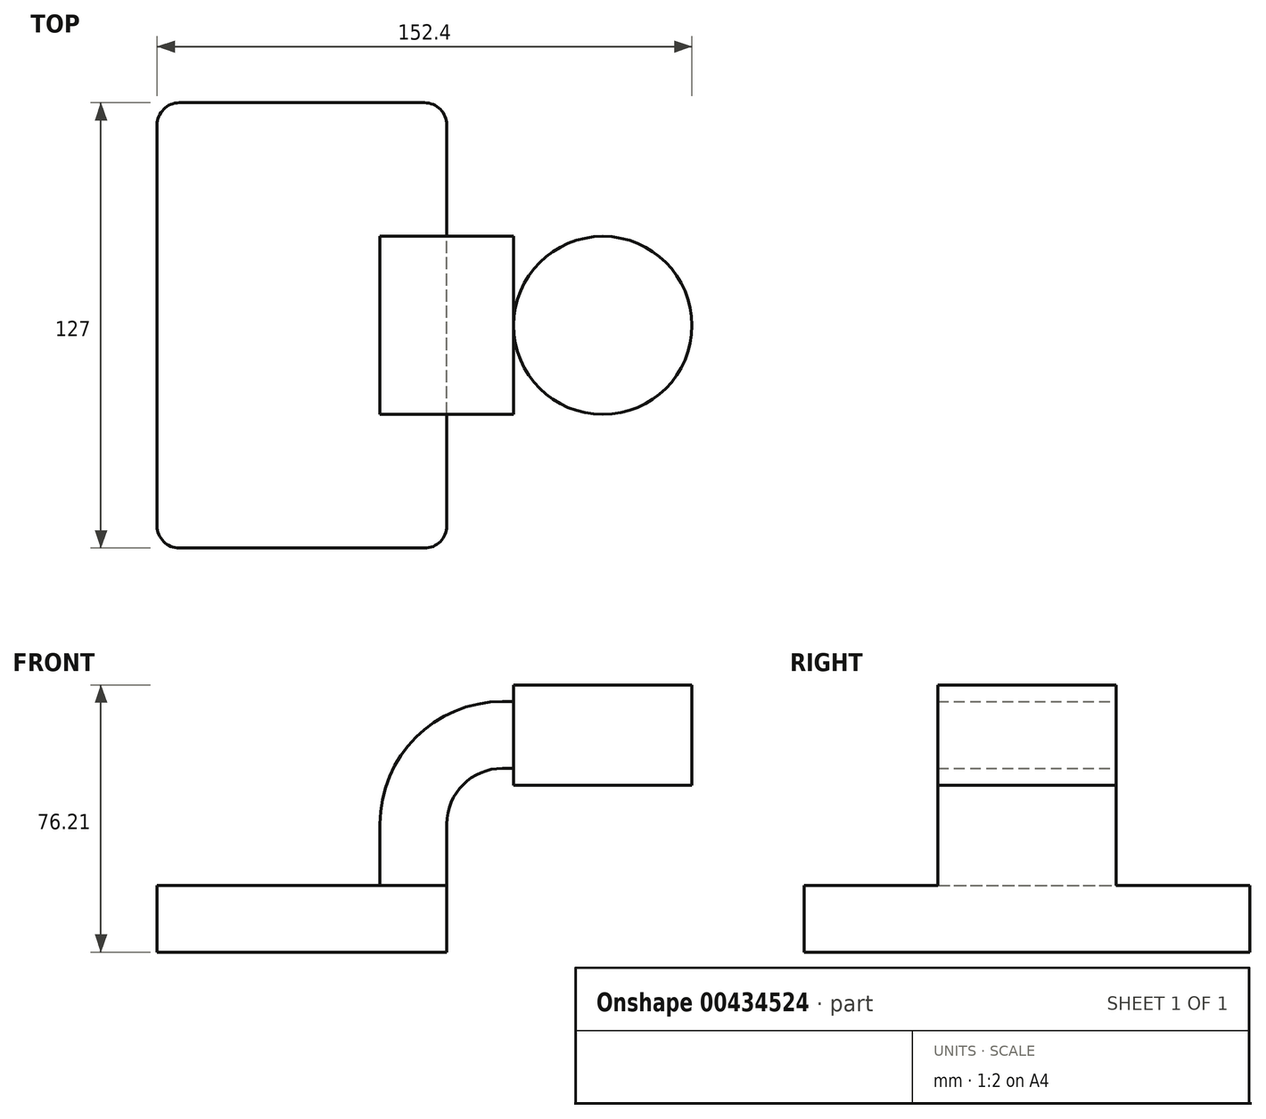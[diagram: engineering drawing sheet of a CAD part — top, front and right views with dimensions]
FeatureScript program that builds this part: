
annotation { "Feature Type Name" : "Feature", "Feature Type Description" : "" }
export const myFeature = defineFeature(function(context is Context, id is Id, definition is map)
    precondition{}
    {
        {
            var Q0;
            Q0=qCreatedBy(makeId("Front.planeOp"),FACE);
            var sketch = newSketch(context, id + "F0", { "sketchPlane" : qUnion([Q0])});
            skLineSegment(sketch, "E0.bottom", {"start": v(-41.28, 9.52) * mm, "end": v(41.27, 9.53) * mm});
            skLineSegment(sketch, "E0.top", {"start": v(-41.28, -9.53) * mm, "end": v(41.28, -9.53) * mm});
            skLineSegment(sketch, "E0.left", {"start": v(-41.28, 9.52) * mm, "end": v(-41.27, -9.53) * mm});
            skLineSegment(sketch, "E0.right", {"start": v(41.28, 9.53) * mm, "end": v(41.28, -9.52) * mm});
            skPoint(sketch, "E0.middle", {"position": v(0, 0) * mm});
            skLineSegment(sketch, "E1.bottom", {"start": v(111.13, 66.68) * mm, "end": v(60.33, 66.68) * mm});
            skLineSegment(sketch, "E1.top", {"start": v(111.13, 38.1) * mm, "end": v(60.33, 38.1) * mm});
            skLineSegment(sketch, "E1.left", {"start": v(111.13, 66.68) * mm, "end": v(111.13, 38.1) * mm});
            skLineSegment(sketch, "E1.right", {"start": v(60.33, 66.68) * mm, "end": v(60.33, 38.1) * mm});
            skPoint(sketch, "E1.middle", {"position": v(85.73, 52.39) * mm});
            skLineSegment(sketch, "E2", {"start": v(41.27, 9.53) * mm, "end": v(41.27, 27) * mm});
            skArc(sketch, "E3", {"start": v(41.27, 27) * mm, "mid": v(45.92, 38.23) * mm, "end": v(57.15, 42.88) * mm});
            skLineSegment(sketch, "E4", {"start": v(57.15, 42.88) * mm, "end": v(85.72, 42.88) * mm});
            skLineSegment(sketch, "E5.0", {"start": v(57.15, 61.93) * mm, "end": v(85.73, 61.93) * mm});
            skArc(sketch, "E5.1", {"start": v(22.22, 27) * mm, "mid": v(32.45, 51.7) * mm, "end": v(57.15, 61.93) * mm});
            skLineSegment(sketch, "E5.2", {"start": v(22.22, 9.53) * mm, "end": v(22.22, 27) * mm});
            skLineSegment(sketch, "E6", {"start": v(85.73, 38.1) * mm, "end": v(85.73, 66.68) * mm});
            skFitSpline(sketch, "E7", {"points": [v(-41.28, 9.53) * mm, v(60.33, 66.68) * mm], "startDerivative": vector(23.41, 107.43) * mm, "endDerivative": vector(122.33, -14.19) * mm});
            skSolve(sketch);
        }
        {
            var Q0;
            Q0=makeQuery(id+"F0.imprint","IMPRINT",FACE,{"disambiguationData":[TD([[makeQuery(id+"F0.imprint","IMPRINT",EDGE,{"derivedFrom":sQuery(id+"F0.wireOp",EDGE,"E0.top")}),1.0]])]});
            extrude(context, id + "F1", {"entities" : qUnion([Q0]), "endBound" : BoundingType.SYMMETRIC, "depth" : 127 * mm});
        }
        {
            var Q0;
            {var subQ1=sQuery(id+"F0.wireOp",EDGE,"E2");Q0=makeQuery(id+"F0.imprint","IMPRINT",FACE,{"disambiguationData":[TD([[makeQuery(id+"F0.imprint","IMPRINT",EDGE,{"derivedFrom":subQ1}),1.0]])]});}
            extrude(context, id + "F2", {"entities" : qUnion([Q0]), "operationType" : NewBodyOperationType.ADD, "endBound" : BoundingType.SYMMETRIC, "depth" : 50.8 * mm});
        }
        {
            var Q0;
            {var subQ0=sQuery(id+"F0.wireOp",EDGE,"E5.1");Q0=makeQuery(id+"F0.imprint","IMPRINT",FACE,{"disambiguationData":[TD([[makeQuery(id+"F0.imprint","IMPRINT",EDGE,{"derivedFrom":subQ0}),1.0]])]});}
            extrude(context, id + "F3", {"entities" : qUnion([Q0]), "operationType" : NewBodyOperationType.ADD, "endBound" : BoundingType.SYMMETRIC, "depth" : 15.88 * mm});
        }
        {
            var Q0;
            {var subQ0=sQuery(id+"F0.wireOp",EDGE,"E1.left");Q0=makeQuery(id+"F0.imprint","IMPRINT",FACE,{"disambiguationData":[TD([[makeQuery(id+"F0.imprint","IMPRINT",EDGE,{"derivedFrom":subQ0}),-1.0]])]});}
            var Q1;
            Q1=sQuery(id+"F0.wireOp",EDGE,"E6");
            revolve(context, id + "F4", {"operationType" : NewBodyOperationType.ADD, "entities" : qUnion([Q0]), "axis" : qUnion([Q1]), "revolveType" : RevolveType.FULL});
        }
        {
            var Q0;
            Q0=makeQuery(id+"F1.opExtrude","CAP_EDGE",EDGE,{"disambiguationData":[OSD([sQuery(id+"F0.wireOp",EDGE,"E0.left")])],"isStart":false});
            var Q1;
            Q1=makeQuery(id+"F1.opExtrude","CAP_EDGE",EDGE,{"disambiguationData":[OSD([sQuery(id+"F0.wireOp",EDGE,"E0.left")])],"isStart":true});
            var Q2;
            Q2=makeQuery(id+"F1.opExtrude","CAP_EDGE",EDGE,{"disambiguationData":[OSD([sQuery(id+"F0.wireOp",EDGE,"E0.right")])],"isStart":false});
            var Q3;
            Q3=makeQuery(id+"F1.opExtrude","CAP_EDGE",EDGE,{"disambiguationData":[OSD([sQuery(id+"F0.wireOp",EDGE,"E0.right")])],"isStart":true});
            fillet(context, id + "F5", {"entities" : qUnion([Q0, Q1, Q2, Q3]), "radius" : 6.35 * mm, "tangentPropagation" : true, "allowEdgeOverflow" : false});
        }
    });
